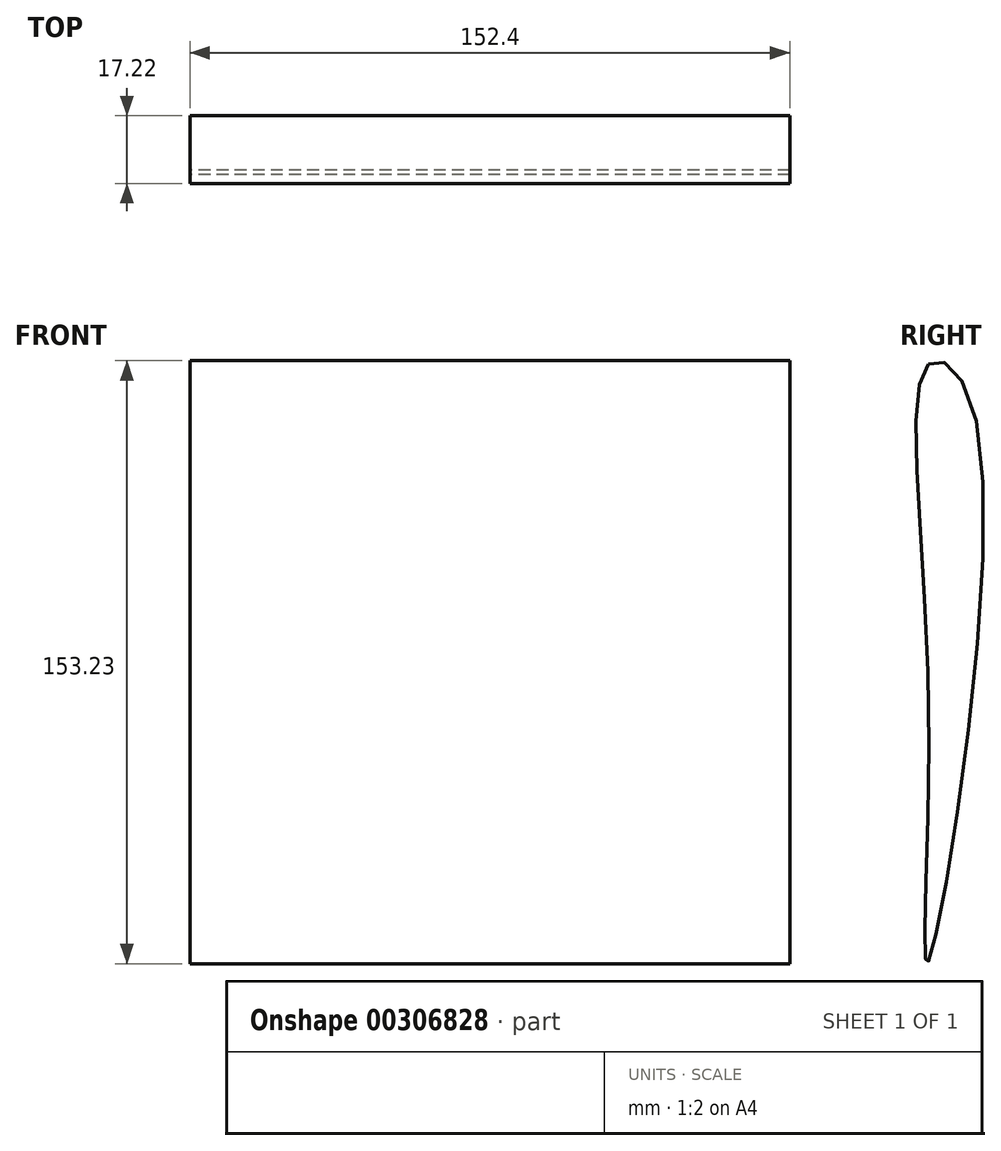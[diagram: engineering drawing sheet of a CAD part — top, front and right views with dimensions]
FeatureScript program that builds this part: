
annotation { "Feature Type Name" : "Feature", "Feature Type Description" : "" }
export const myFeature = defineFeature(function(context is Context, id is Id, definition is map)
    precondition{}
    {
        {
            var Q0;
            Q0=qCreatedBy(makeId("Right.planeOp"),FACE);
            var sketch = newSketch(context, id + "F0", { "sketchPlane" : qUnion([Q0])});
            skFitSpline(sketch, "E0", {"points": [v(-2.03, 75.34) * mm, v(9.75, 62.3) * mm, v(-2.03, -76.46) * mm, v(-2.03, -8.77) * mm, v(-2.03, 75.34) * mm]});
            skSolve(sketch);
        }
        {
            var Q0;
            Q0 = qSketchRegion(id + "F0", true);
            extrude(context, id + "F1", {"entities" : qUnion([Q0]), "depth" : 76.2 * mm, "hasSecondDirection" : true, "secondDirectionOppositeDirection" : true, "secondDirectionDepth" : 76.2 * mm});
        }
    });
